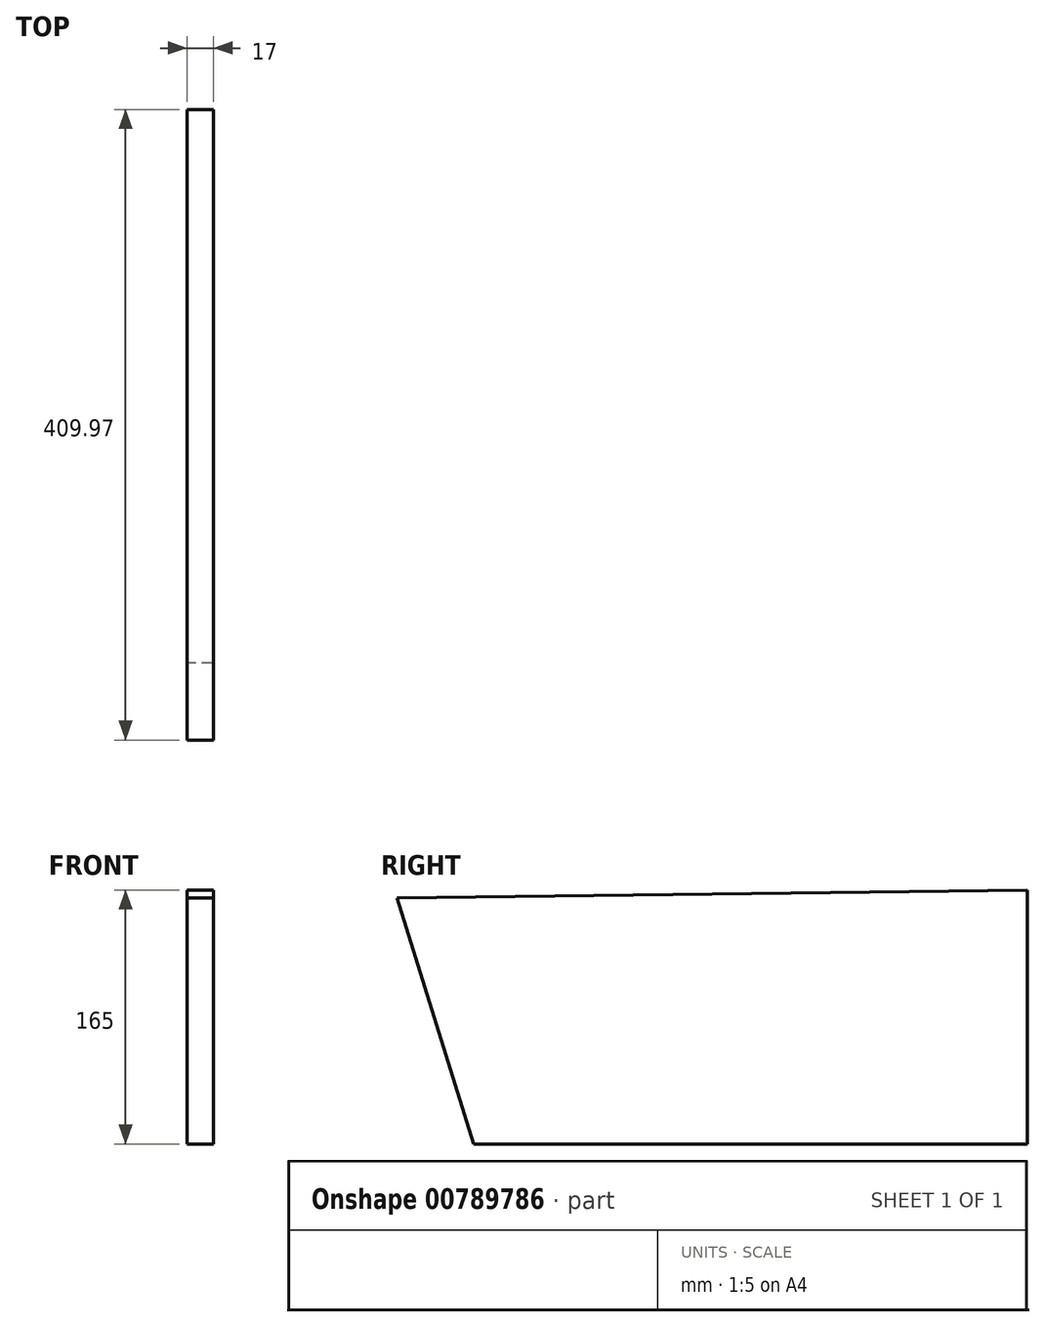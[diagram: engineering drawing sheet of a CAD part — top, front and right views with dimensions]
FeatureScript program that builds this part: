
annotation { "Feature Type Name" : "Feature", "Feature Type Description" : "" }
export const myFeature = defineFeature(function(context is Context, id is Id, definition is map)
    precondition{}
    {
        {
            var Q0;
            Q0=qCreatedBy(makeId("Right.planeOp"),FACE);
            var sketch = newSketch(context, id + "F0", { "sketchPlane" : qUnion([Q0])});
            skLineSegment(sketch, "E0.top", {"start": v(-5.48, -130.4) * mm, "end": v(354.52, -130.4) * mm});
            skLineSegment(sketch, "E1", {"start": v(354.52, -130.4) * mm, "end": v(354.52, 34.6) * mm});
            skPoint(sketch, "E2.end.orphan", {"position": v(-55.45, 29.6) * mm});
            skLineSegment(sketch, "E3", {"start": v(-55.45, 29.6) * mm, "end": v(354.52, 34.6) * mm});
            skLineSegment(sketch, "E4", {"start": v(-5.48, -130.4) * mm, "end": v(-55.45, 29.6) * mm});
            skSolve(sketch);
        }
        {
            var Q0;
            Q0 = qSketchRegion(id + "F0", true);
            extrude(context, id + "F1", {"entities" : qUnion([Q0]), "depth" : 17 * mm, "offsetDistance" : 25 * mm});
        }
    });
